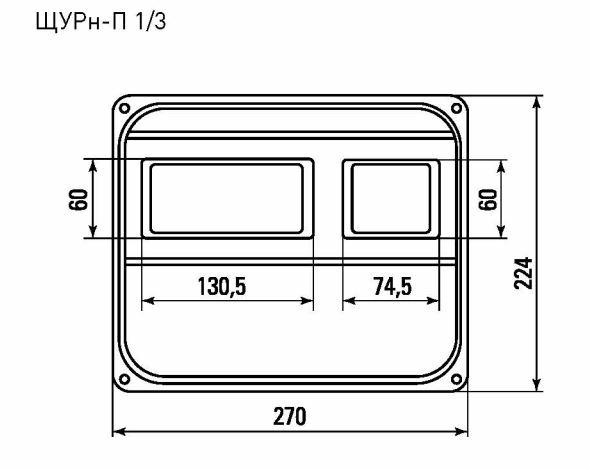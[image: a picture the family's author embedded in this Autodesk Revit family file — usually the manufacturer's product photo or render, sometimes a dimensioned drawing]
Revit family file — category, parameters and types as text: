
# Revit family: EKF_EE_ПанельМонтажная_PROxima
name_source: partatom
category: Электрооборудование
units: mm (PartAtom-declared; Revit-internal decimal feet)

## family parameters
Всегда вертикально = Нет
На основе рабочей плоскости = Да
Общий = Да
При загрузке вырезать с полостями = Нет
Размер круглого соединителя = Использовать диаметр
Тип детали = Силовой щит
Точка расчета площади = Нет

## types (27) — shared parameters
ADSK_Единица измерения = шт.
ADSK_Завод-изготовитель = EKF
ADSK_Количество = 1
ADSK_Материал = Сталь_Оцинкованная
D = 7 мм
Глубина_Загиба = 20 мм
Изготовитель = EKF
Отступ = 16 мм
Серия номенклатуры = Unit PROxima
Степень защиты IP = -
ТВ = EKF_2
Тип установки = -
zero-valued in all types: ADSK_Масса, Отметка по умолчанию

## per-type parameters (varying)
| type | ADSK_Код изделия | ADSK_Марка | ADSK_Обозначение | ADSK_Размер_Высота | ADSK_Размер_Глубина | ADSK_Размер_Ширина | T | Глубина | Загиб1 | ЗагибШирина | Отв_Кол | Отступ2 | Тип |
| Панель монтажная (160x360) к ВРУ Unit (Вх450хГ) EKF PROxima | mb15-04-03 | Панель монтажная (160x360) | Панель монтажная (160x360) | 160 мм | 19 мм | 360 мм | 1 мм | 10 мм | Нет | 19 мм | 2 | 11 мм | 43 мм |
| Панель монтажная (160x510) к ВРУ Unit и ЩО-70 (Вх600хГ) EKF PROxima | mb15-06-01-02 | Панель монтажная (160x510) | Панель монтажная (160x510) | 160 мм | 29 мм | 510 мм | 1 мм | 10 мм | Да | 19 мм | 2 | 11 мм | 44 мм |
| Панель монтажная (160x710) к ВРУ Unit и ЩО-70 (Вх800хГ) EKF PROxima | mb15-08-01-02 | Панель монтажная (160x710) | Панель монтажная (160x710) | 160 мм | 29 мм | 710 мм | 1 мм | 10 мм | Да | 19 мм | 2 | 11 мм | 45 мм |
| Панель монтажная (160x910) к ВРУ Unit и ЩО-70 (Вх1000хГ) EKF PROxima | mb15-10-01-02 | Панель монтажная (160x910) | Панель монтажная (160x910) | 160 мм | 29 мм | 910 мм | 1 мм | 10 мм | Да | 19 мм | 2 | 11 мм | 46 мм |
| Панель монтажная (160х360х2) к ВРУ Unit (Bх450хГ) EKF PROxima | mb15-04-03s | Панель монтажная (160х360х2) | Панель монтажная (160х360х2) | 160 мм | 20 мм | 360 мм | 2 мм | 28.5 мм | Нет | 20 мм | 2 | 12.5 мм | 47 мм |
| Панель монтажная (160х510х2) к ВРУ Unit и ЩО-70 (Bх600хГ) EKF PROxima | mb15-06-01-02s | Панель монтажная (160х510х2) | Панель монтажная (160х510х2) | 160 мм | 20 мм | 510 мм | 2 мм | 28.5 мм | Нет | 20 мм | 2 | 12.5 мм | 48 мм |
| Панель монтажная (160х710х2) к ВРУ Unit (Bх800хГ) и ЩО-70 Unit EKF PROxima | mb15-08-01-02s | Панель монтажная (160х710х2) | Панель монтажная (160х710х2) | 160 мм | 20 мм | 710 мм | 2 мм | 28.5 мм | Нет | 20 мм | 2 | 12.5 мм | 49 мм |
| Панель монтажная (220x360) к ВРУ Unit (Вх450хГ) EKF PROxima | mb15-04-04 | Панель монтажная (220x360) | Панель монтажная (220x360) | 220 мм | 29 мм | 360 мм | 1 мм | 10 мм | Да | 19 мм | 2 | 11 мм | 50 мм |
| Панель монтажная (220x510) к ВРУ Unit и ЩО-70 (Вх600хГ) EKF PROxima | mb15-05-04 | Панель монтажная (220x510) | Панель монтажная (220x510) | 220 мм | 29 мм | 510 мм | 1 мм | 10 мм | Да | 19 мм | 2 | 11 мм | 51 мм |
| Панель монтажная (220x710) к ВРУ Unit и ЩО-70 (Вх800хГ) EKF PROxima | mb15-08-02-01 | Панель монтажная (220x710) | Панель монтажная (220x710) | 220 мм | 29 мм | 710 мм | 1 мм | 10 мм | Да | 19 мм | 2 | 11 мм | 52 мм |
| Панель монтажная (220x910) к ВРУ Unit и ЩО-70 (Вх1000хГ) EKF PROxima | mb15-10-02-01 | Панель монтажная (220x910) | Панель монтажная (220x910) | 220 мм | 28.5 мм | 910 мм | 1 мм | 10 мм | Да | 18.5 мм | 2 | 12.5 мм | 53 мм |
| Панель монтажная (220х360х2) к ВРУ Unit (Bх450хГ) EKF PROxima | mb15-04-04s | Панель монтажная (220х360х2) | Панель монтажная (220х360х2) | 220 мм | 20 мм | 360 мм | 2 мм | 28.5 мм | Нет | 20 мм | 2 | 12.5 мм | 54 мм |
| Панель монтажная (220х510х2) к ВРУ Unit и ЩО-70 (Bх600хГ) EKF PROxima | mb15-05-04s | Панель монтажная (220х510х2) | Панель монтажная (220х510х2) | 220 мм | 20 мм | 510 мм | 2 мм | 28.5 мм | Нет | 20 мм | 2 | 12.5 мм | 55 мм |
| Панель монтажная (220х710х2) к ВРУ Unit (Bх800хГ) и ЩО-70 Unit EKF PROxima | mb15-08-02-01s | Панель монтажная (220х710х2) | Панель монтажная (220х710х2) | 220 мм | 20 мм | 710 мм | 2 мм | 10 мм | Нет | 20 мм | 2 | 12.5 мм | 56 мм |
| Панель монтажная (480x360) к ВРУ Unit (Вх450хГ) EKF PROxima | mb15-08-01-04 | Панель монтажная (480x360) | Панель монтажная (480x360) | 480 мм | 28.5 мм | 360 мм | 1.5 мм | 10 мм | Да | 18.5 мм | 2 | 11.5 мм | 57 мм |
| Панель монтажная (480x510) к ВРУ Unit и ЩО-70 (Вх600хГ) EKF PROxima | mb15-08-01-05 | Панель монтажная (480x510) | Панель монтажная (480x510) | 480 мм | 28.5 мм | 510 мм | 1.5 мм | 10 мм | Да | 18.5 мм | 2 | 11.5 мм | 58 мм |
| Панель монтажная (480x710) к ВРУ Unit и ЩО-70 (Вх800хГ) EKF PROxima | mb15-08-01-06 | Панель монтажная (480x710) | Панель монтажная (480x710) | 480 мм | 28.5 мм | 710 мм | 1.5 мм | 10 мм | Да | 18.5 мм | 2 | 11.5 мм | 59 мм |
| Панель монтажная (480x910) к ВРУ Unit и ЩО-70 (Вх1000хГ) EKF PROxima | mb15-10-01-05 | Панель монтажная (480x910) | Панель монтажная (480x910) | 480 мм | 28.5 мм | 910 мм | 1.5 мм | 10 мм | Да | 18.5 мм | 2 | 11.5 мм | 60 мм |
| Панель монтажная (480х360х2) к ВРУ Unit (Bх450хГ) EKF PROxima | mb15-08-01-04s | Панель монтажная (480х360х2) | Панель монтажная (480х360х2) | 480 мм | 20 мм | 360 мм | 2 мм | 28.5 мм | Нет | 20 мм | 2 | 12.5 мм | 61 мм |
| Панель монтажная (480х510х2) к ВРУ Unit и ЩО-70 (Bх600хГ) EKF PROxima | mb15-08-01-05s | Панель монтажная (480х510х2) | Панель монтажная (480х510х2) | 480 мм | 20 мм | 510 мм | 2 мм | 28.5 мм | Нет | 20 мм | 2 | 12.5 мм | 62 мм |
| Панель монтажная (480х710х2) к ВРУ Unit (Bх800хГ) и ЩО-70 Unit EKF PROxima | mb15-08-01-06s | Панель монтажная (480х710х2) | Панель монтажная (480х710х2) | 480 мм | 20 мм | 710 мм | 2 мм | 28.5 мм | Нет | 20 мм | 2 | 12.5 мм | 63 мм |
| Панель монтажная (1800х710х2) к ВРУ Unit (2000х800хГ) и ЩО-70 Unit EKF PROxima | mb15-18-71s | Панель монтажная (1800х710х2) | Панель монтажная (1800х710х2) | 1800 мм | 32.5 мм | 710 мм | 2 мм | 15 мм | Да | 17.5 мм | 3 | 16.5 мм | 42 мм |
| Панель монтажная (1800х510х2) к ВРУ Unit (2000х600хГ) EKF PROxima | mb15-18-51s | Панель монтажная (1800х510х2) | Панель монтажная (1800х510х2) | 1800 мм | 32.5 мм | 510 мм | 2 мм | 15 мм | Да | 17.5 мм | 3 | 16.5 мм | 41 мм |
| Панель монтажная (1800х360х2) к ВРУ Unit (2000х450хГ) EKF PROxima | mb15-18-45s | Панель монтажная (1800х360х2) | Панель монтажная (1800х360х2) | 1800 мм | 32.5 мм | 360 мм | 2 мм | 15 мм | Да | 17.5 мм | 3 | 16.5 мм | 40 мм |
| Панель монтажная (1600х710х2) к ВРУ Unit и ЩО-70 (1800х800хГ) EKF PROxima | mb15-16-71s | Панель монтажная (1600х710х2) | Панель монтажная (1600х710х2) | 1600 мм | 32.5 мм | 710 мм | 2 мм | 15 мм | Да | 17.5 мм | 3 | 21.5 мм | 39 мм |
| Панель монтажная (1600х510х2) к ВРУ Unit и ЩО-70 (1800х600хГ) EKF PROxima | mb15-16-51s | Панель монтажная (1600х510х2) | Панель монтажная (1600х510х2) | 1600 мм | 32.5 мм | 510 мм | 2 мм | 15 мм | Да | 17.5 мм | 3 | 21.5 мм | 38 мм |
| Панель монтажная (1600х360х2) к ВРУ Unit (1800х450хГ) EKF PROxima | mb15-16-45s | Панель монтажная (1600х360х2) | Панель монтажная (1600х360х2) | 1600 мм | 32.5 мм | 360 мм | 2 мм | 15 мм | Да | 17.5 мм | 3 | 21.5 мм | 37 мм |

note: column(s) folded — value = type name in every type: ADSK_Наименование
